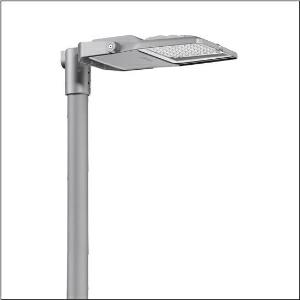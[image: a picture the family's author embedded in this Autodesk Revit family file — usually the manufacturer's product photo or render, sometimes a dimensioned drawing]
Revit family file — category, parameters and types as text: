
# Revit family: floodlight_fl_21_iq_mini___pl43_5xa7771b4a3a_ae81
name_source: partatom
category: Lighting Fixtures
units: mm (PartAtom-declared; Revit-internal decimal feet)

## family parameters
Cut with Voids When Loaded = No
Host = Face
Light Source = No
Part Type = Normal
Room Calculation Point = No
Round Connector Dimension = Use Diameter
Shared = No

## types (1)
- --- (1 x LED, 6660 lm, 45.5 W, 4000K)
    Apparent Load = 46 VA
    CIE Flux Codes = 27 78 99 100 100
    Color Rendering = 70
    Color Temperature = 4000K
    Default Elevation = 1800 mm
    Description = Floodlight FL 21 iQ mini, floodlight, primary light control with lens, of PMMA, primary optical cover: protective disc, of toughened safety glass, transparent, light distribution: PL43, light emission: direct distribution, installation type: surface-mounted, LED, High Power LED, rated luminous flux: 6.660lm, luminous efficacy: 146lm/W, light colour: 740, colour temperature: 4000K, control: Auto-Match, Temp-Guard, Lumen-Switch, Night-Set, Smart-Wire, Light-Fading, Desk-Remote (wireless, voltage-free reading and setting of iQ features in the workshop via application-optimized NFC function/RFID function), optimised constant luminous flux control (CLO 2.0), with terminal, 6-pole, mains connection: 220..240V, AC, 50/60Hz, start of lifetime: 46W, end of service life: 48W, reduction: 22W, luminaire housing, of diecast aluminium, powder-coated, Siteco® metallic grey (DB 702S), corrosivity category C5 mid according to DIN EN ISO 12944, sealing non-destructively replaceable, please order mast flange separately, mast bracket, of steel, galvanised, powder-coated, Siteco® metallic grey (DB 702S), protection rating (complete): IP66, insulation class (complete): insulation class II (safety insulation), certification: CE, ENEC, VDE, protection symbol: D, impact resistance: IK08, permissible operating ambient temperature: -40..+40°C, permissible operating ambient temperature for outdoor applications: -40..+50°C, standard: DIN EN 12944, LABS conformity tested according to VDMA 24364:2018-05, packaging unit: 1 piece

Light Distribution: PL43
    Height = 70 mm
    Lamp = 1 x LED
    Lamp Light Flux = 6660 lm
    Lamp Power = 45.5 W
    Lamp count = 1
    Length = 485 mm
    Luminous efficacy = 146 lm/W
    Manufacturer = Siteco
    ModVariant = No
    Model = 5XA7771B4A3A
    Number of Poles = 1
    OnlyDefault = Yes
    Power Factor = 1
    Product Name = Floodlight FL 21 iQ mini | PL43
    Product group = floodlight | pylon annexe
    ProductGroupID = 6200
    Protection Class = Protection class II
    Protection Degree = IP 66
    RLX_Detail_Level = 1
    RLX_Emergency_Light_Flux = 0 lm
    RLX_Emergency_Type = 0
    RLX_Emergency_Type_DB = No
    RlxData = <blob elided: 101025 chars, md5=239b26cf>
    Socket = socket
    Standby Power = 0 W
    System Light Flux = 6660 lm
    System Power = 46 W
    Type Comments = factory setting: luminous flux: 100 % | dim-lin: 254 | 463 mA
    Type Image = l_1007125.jpg
    URL = http://relux.com
    VarID = @adj_113049
    Voltage = 0 V
    Weight = 0.00 kg
    Width = 337 mm

## geometry (parser evidence)
native form markers: Blend x4, Sweep x12
no freeform markers — native parametric forms only
